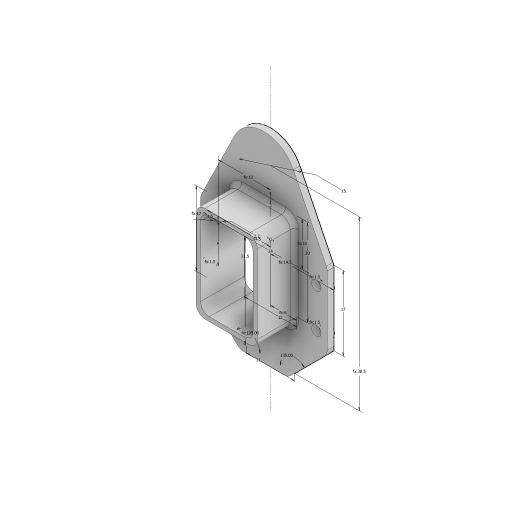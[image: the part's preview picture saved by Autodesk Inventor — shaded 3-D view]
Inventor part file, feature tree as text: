
AUTODESK INVENTOR PART (.ipt)
format: ipt  version: 2023 (Build 270158000, 158)  size: 204,800 bytes
history: native  units: in
note: dims shown in document units (in); Inventor stores cm internally (conversion verified against a paired STEP export)
features: extrude x3, fillet x2, sketch x1
ambient origin geometry x8: Origin, YZ Plane, XZ Plane, XY Plane, X Axis, Y Axis, Z Axis, Center Point
bodies: Solid1 (feature_tree)
feature tree (6):
  sketch  "Sketch1"  dims[d0=0.4724in d1=0.7874in d2=0.3937in d3=0.2362in d4=0.4331in d5=0.8465in d6=0.0in d7=135.0deg d8=135.0deg d9=0.5709in d10=0.5709in d11=0.5906in d12=1.5157in d13=0.6693in d14=0.6693in d15=0.0866in d16=0.7874in d18=0.3543in d19=0.7874in d21=0.9449in d24=0.4724in d25=0.0in d28=0.0591in d29=0.0in d30=0.0394in d31=0.3937in d32=0.0in d33=0.0787in d34=0.0591in d35=0.0591in d36=0.0591in d37=0.0591in d38=0.1378in d39=0.0in d40=0.0394in]
  extrude  "Extrusion1"  Depth=0.7874in
  extrude  "Extrusion2"  Depth=0.3937in
  fillet  "Fillet1"  Radius=0.2362in
  extrude  "Extrusion3"  Depth=0.0394in
  fillet  "Fillet2"  Radius=0.8465in
